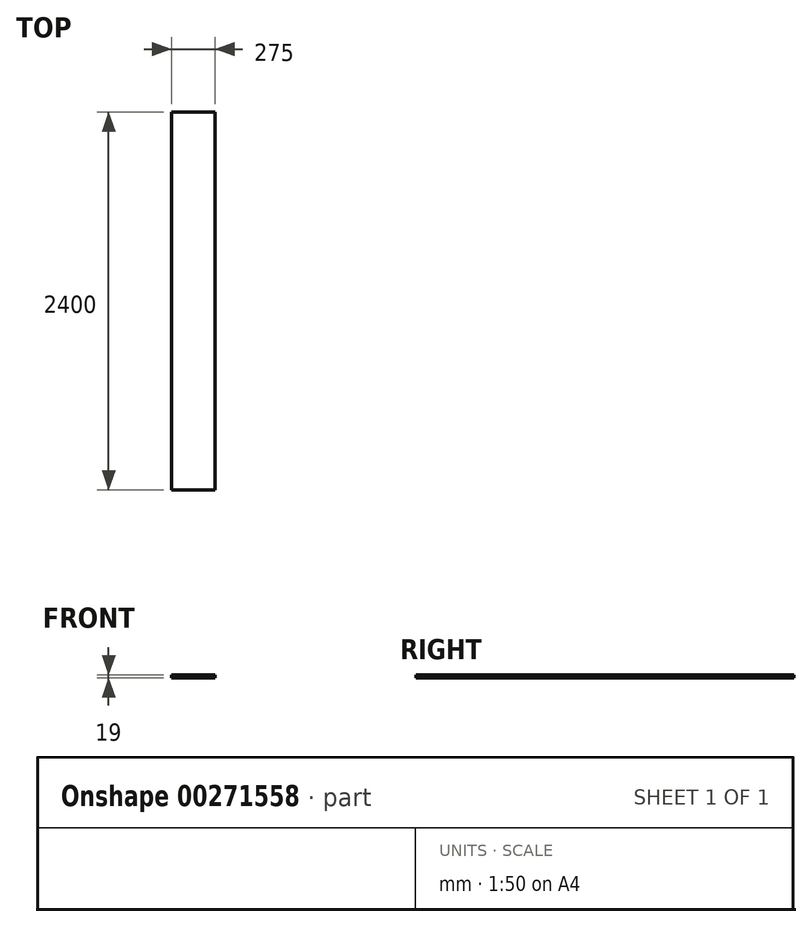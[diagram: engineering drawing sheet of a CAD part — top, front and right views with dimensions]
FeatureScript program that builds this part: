
annotation { "Feature Type Name" : "Feature", "Feature Type Description" : "" }
export const myFeature = defineFeature(function(context is Context, id is Id, definition is map)
    precondition{}
    {
        {
            var Q0;
            Q0=qCreatedBy(makeId("Top.planeOp"),FACE);
            var sketch = newSketch(context, id + "F0", { "sketchPlane" : qUnion([Q0])});
            skLineSegment(sketch, "E0.bottom", {"start": v(137.5, -1200) * mm, "end": v(-137.5, -1200) * mm});
            skLineSegment(sketch, "E0.top", {"start": v(137.5, 1200) * mm, "end": v(-137.5, 1200) * mm});
            skLineSegment(sketch, "E0.left", {"start": v(137.5, -1200) * mm, "end": v(137.5, 1200) * mm});
            skLineSegment(sketch, "E0.right", {"start": v(-137.5, -1200) * mm, "end": v(-137.5, 1200) * mm});
            skPoint(sketch, "E0.middle", {"position": v(0, 0) * mm});
            skSolve(sketch);
        }
        {
            var Q0;
            Q0 = qSketchRegion(id + "F0", true);
            extrude(context, id + "F1", {"entities" : qUnion([Q0]), "depth" : 19 * mm});
        }
    });
